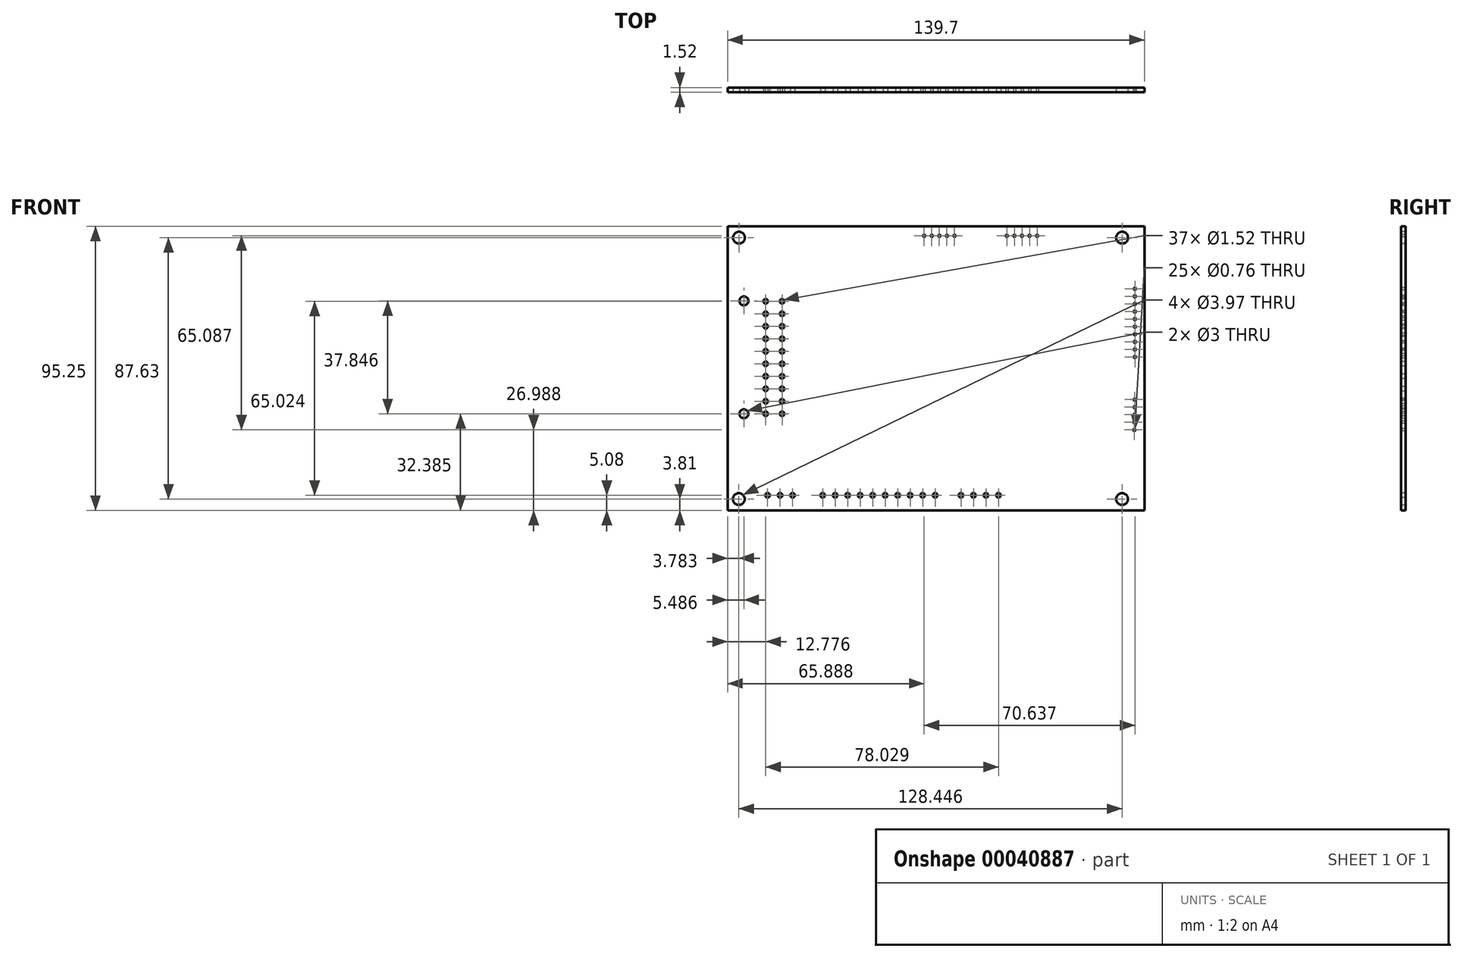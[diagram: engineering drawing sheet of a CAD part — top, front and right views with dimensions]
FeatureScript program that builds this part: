
annotation { "Feature Type Name" : "Feature", "Feature Type Description" : "" }
export const myFeature = defineFeature(function(context is Context, id is Id, definition is map)
    precondition{}
    {
        {
            var Q0;
            Q0=qCreatedBy(makeId("Front.planeOp"),FACE);
            var sketch = newSketch(context, id + "F0", { "sketchPlane" : qUnion([Q0])});
            skLineSegment(sketch, "E0.bottom", {"start": v(0, 0) * mm, "end": v(139.7, 0) * mm});
            skLineSegment(sketch, "E0.top", {"start": v(0, 95.25) * mm, "end": v(139.7, 95.25) * mm});
            skLineSegment(sketch, "E0.left", {"start": v(0, 0) * mm, "end": v(0, 95.25) * mm});
            skLineSegment(sketch, "E0.right", {"start": v(139.7, 0) * mm, "end": v(139.7, 95.25) * mm});
            skLineSegment(sketch, "E1", {"start": v(0, 47.62) * mm, "end": v(139.7, 47.62) * mm, "construction": true});
            skLineSegment(sketch, "E2", {"start": v(69.85, 95.25) * mm, "end": v(69.85, 0) * mm, "construction": true});
            skSolve(sketch);
        }
        {
            var Q0;
            Q0 = qSketchRegion(id + "F0", true);
            extrude(context, id + "F1", {"entities" : qUnion([Q0]), "depth" : 1.52 * mm});
        }
        {
            var Q0;
            Q0=makeQuery(id+"F1.opExtrude","CAP_FACE",FACE,{"disambiguationData":[OSD([sQuery(id+"F0.wireOp",EDGE,"E0.bottom"),sQuery(id+"F0.wireOp",EDGE,"E0.top"),sQuery(id+"F0.wireOp",EDGE,"E0.left"),sQuery(id+"F0.wireOp",EDGE,"E0.right")])],"isStart":false});
            var sketch = newSketch(context, id + "F2", { "sketchPlane" : qUnion([Q0])});
            skCircle(sketch, "E3", {"center": v(3.8, 91.44) * mm, "radius": 1.98 * mm});
            skCircle(sketch, "E4.1.0.0", {"center": v(132.23, 91.44) * mm, "radius": 1.98 * mm});
            skLineSegment(sketch, "E4.direction1", {"start": v(3.8, 91.44) * mm, "end": v(132.23, 91.44) * mm, "construction": true});
            skCircle(sketch, "E5.1.0.0", {"center": v(3.78, 3.81) * mm, "radius": 1.98 * mm});
            skLineSegment(sketch, "E5.direction1", {"start": v(3.8, 91.44) * mm, "end": v(3.78, 3.81) * mm, "construction": true});
            skCircle(sketch, "E6.1.0.0", {"center": v(132.21, 3.81) * mm, "radius": 1.98 * mm});
            skLineSegment(sketch, "E6.direction1", {"start": v(3.78, 3.81) * mm, "end": v(132.21, 3.81) * mm, "construction": true});
            skSolve(sketch);
        }
        {
            var Q0;
            Q0 = qSketchRegion(id + "F2", true);
            extrude(context, id + "F3", {"entities" : qUnion([Q0]), "operationType" : NewBodyOperationType.REMOVE, "oppositeDirection" : true, "depth" : 25.4 * mm});
        }
        {
            var Q0;
            Q0=makeQuery(id+"F2.imprint","IMPRINT",FACE,{"disambiguationData":[TD([[makeQuery(id+"F2.imprint","IMPRINT",EDGE,{"derivedFrom":sQuery(id+"F2.wireOp",EDGE,"E3")}),-1.0]])]});
            var sketch = newSketch(context, id + "F4", { "sketchPlane" : qUnion([Q0])});
            skCircle(sketch, "E7", {"center": v(136.53, 74.3) * mm, "radius": 0.38 * mm});
            skCircle(sketch, "E8.0.1.0", {"center": v(136.53, 71.75) * mm, "radius": 0.38 * mm});
            skCircle(sketch, "E8.0.2.0", {"center": v(136.53, 69.22) * mm, "radius": 0.38 * mm});
            skCircle(sketch, "E8.0.3.0", {"center": v(136.53, 66.67) * mm, "radius": 0.38 * mm});
            skCircle(sketch, "E8.0.4.0", {"center": v(136.53, 64.13) * mm, "radius": 0.38 * mm});
            skCircle(sketch, "E8.0.5.0", {"center": v(136.53, 61.6) * mm, "radius": 0.38 * mm});
            skCircle(sketch, "E8.0.6.0", {"center": v(136.53, 59.05) * mm, "radius": 0.38 * mm});
            skCircle(sketch, "E8.0.7.0", {"center": v(136.53, 56.51) * mm, "radius": 0.38 * mm});
            skCircle(sketch, "E8.0.8.0", {"center": v(136.53, 53.97) * mm, "radius": 0.38 * mm});
            skCircle(sketch, "E8.0.9.0", {"center": v(136.53, 51.44) * mm, "radius": 0.38 * mm});
            skLineSegment(sketch, "E8.direction1", {"start": v(136.53, 74.3) * mm, "end": v(186.53, 74.3) * mm, "construction": true});
            skLineSegment(sketch, "E8.direction2", {"start": v(136.53, 74.3) * mm, "end": v(136.53, 71.75) * mm, "construction": true});
            skCircle(sketch, "E9", {"center": v(136.48, 37.15) * mm, "radius": 0.38 * mm});
            skCircle(sketch, "E10.1.0.0", {"center": v(136.45, 34.6) * mm, "radius": 0.38 * mm});
            skCircle(sketch, "E10.2.0.0", {"center": v(136.41, 32.07) * mm, "radius": 0.38 * mm});
            skCircle(sketch, "E10.3.0.0", {"center": v(136.38, 29.53) * mm, "radius": 0.38 * mm});
            skCircle(sketch, "E10.4.0.0", {"center": v(136.35, 26.99) * mm, "radius": 0.38 * mm});
            skLineSegment(sketch, "E10.direction1", {"start": v(136.48, 37.15) * mm, "end": v(136.45, 34.6) * mm, "construction": true});
            skCircle(sketch, "E11", {"center": v(103.76, 92.08) * mm, "radius": 0.38 * mm});
            skCircle(sketch, "E12.1.0.0", {"center": v(101.22, 92.08) * mm, "radius": 0.38 * mm});
            skCircle(sketch, "E12.2.0.0", {"center": v(98.68, 92.08) * mm, "radius": 0.38 * mm});
            skLineSegment(sketch, "E12.direction1", {"start": v(103.76, 92.08) * mm, "end": v(101.22, 92.08) * mm, "construction": true});
            skCircle(sketch, "E13.0.3.0", {"center": v(96.14, 92.08) * mm, "radius": 0.38 * mm});
            skCircle(sketch, "E13.0.4.0", {"center": v(93.6, 92.08) * mm, "radius": 0.38 * mm});
            skCircle(sketch, "E14", {"center": v(76.05, 92.08) * mm, "radius": 0.38 * mm});
            skCircle(sketch, "E15.1.0.0", {"center": v(73.5, 92.08) * mm, "radius": 0.38 * mm});
            skCircle(sketch, "E15.2.0.0", {"center": v(70.97, 92.08) * mm, "radius": 0.38 * mm});
            skCircle(sketch, "E15.3.0.0", {"center": v(68.43, 92.08) * mm, "radius": 0.38 * mm});
            skCircle(sketch, "E15.4.0.0", {"center": v(65.89, 92.08) * mm, "radius": 0.38 * mm});
            skLineSegment(sketch, "E15.direction1", {"start": v(76.05, 92.08) * mm, "end": v(73.5, 92.08) * mm, "construction": true});
            skCircle(sketch, "E16", {"center": v(90.8, 5.08) * mm, "radius": 0.76 * mm});
            skCircle(sketch, "E17.1.0.0", {"center": v(86.61, 5.08) * mm, "radius": 0.76 * mm});
            skCircle(sketch, "E17.2.0.0", {"center": v(82.42, 5.08) * mm, "radius": 0.76 * mm});
            skCircle(sketch, "E17.3.0.0", {"center": v(78.23, 5.08) * mm, "radius": 0.76 * mm});
            skLineSegment(sketch, "E17.direction1", {"start": v(90.8, 5.08) * mm, "end": v(86.61, 5.08) * mm, "construction": true});
            skCircle(sketch, "E18", {"center": v(69.6, 5.08) * mm, "radius": 0.76 * mm});
            skCircle(sketch, "E19.1.0.0", {"center": v(65.4, 5.08) * mm, "radius": 0.76 * mm});
            skCircle(sketch, "E19.2.0.0", {"center": v(61.21, 5.08) * mm, "radius": 0.76 * mm});
            skCircle(sketch, "E19.3.0.0", {"center": v(57.02, 5.08) * mm, "radius": 0.76 * mm});
            skCircle(sketch, "E19.4.0.0", {"center": v(52.83, 5.08) * mm, "radius": 0.76 * mm});
            skCircle(sketch, "E19.5.0.0", {"center": v(48.64, 5.08) * mm, "radius": 0.76 * mm});
            skCircle(sketch, "E19.6.0.0", {"center": v(44.45, 5.08) * mm, "radius": 0.76 * mm});
            skCircle(sketch, "E19.7.0.0", {"center": v(40.26, 5.08) * mm, "radius": 0.76 * mm});
            skCircle(sketch, "E19.8.0.0", {"center": v(36.07, 5.08) * mm, "radius": 0.76 * mm});
            skCircle(sketch, "E19.9.0.0", {"center": v(31.88, 5.08) * mm, "radius": 0.76 * mm});
            skLineSegment(sketch, "E19.direction1", {"start": v(69.6, 5.08) * mm, "end": v(65.4, 5.08) * mm, "construction": true});
            skCircle(sketch, "E20", {"center": v(21.8, 5.08) * mm, "radius": 0.76 * mm});
            skCircle(sketch, "E21.1.0.0", {"center": v(17.6, 5.08) * mm, "radius": 0.76 * mm});
            skCircle(sketch, "E21.2.0.0", {"center": v(13.42, 5.08) * mm, "radius": 0.76 * mm});
            skLineSegment(sketch, "E21.direction1", {"start": v(21.8, 5.08) * mm, "end": v(17.6, 5.08) * mm, "construction": true});
            skCircle(sketch, "E22", {"center": v(18.29, 32.39) * mm, "radius": 0.76 * mm});
            skCircle(sketch, "E23.0.1.0", {"center": v(18.29, 36.58) * mm, "radius": 0.76 * mm});
            skCircle(sketch, "E23.0.2.0", {"center": v(18.29, 40.77) * mm, "radius": 0.76 * mm});
            skCircle(sketch, "E23.0.3.0", {"center": v(18.29, 44.96) * mm, "radius": 0.76 * mm});
            skCircle(sketch, "E23.0.4.0", {"center": v(18.29, 49.15) * mm, "radius": 0.76 * mm});
            skCircle(sketch, "E23.0.5.0", {"center": v(18.29, 53.34) * mm, "radius": 0.76 * mm});
            skCircle(sketch, "E23.0.6.0", {"center": v(18.29, 57.53) * mm, "radius": 0.76 * mm});
            skCircle(sketch, "E23.0.7.0", {"center": v(18.29, 61.72) * mm, "radius": 0.76 * mm});
            skCircle(sketch, "E23.0.8.0", {"center": v(18.29, 65.91) * mm, "radius": 0.76 * mm});
            skCircle(sketch, "E23.0.9.0", {"center": v(18.29, 70.1) * mm, "radius": 0.76 * mm});
            skCircle(sketch, "E23.1.0.0", {"center": v(12.78, 32.39) * mm, "radius": 0.76 * mm});
            skCircle(sketch, "E23.1.1.0", {"center": v(12.78, 36.58) * mm, "radius": 0.76 * mm});
            skCircle(sketch, "E23.1.2.0", {"center": v(12.78, 40.77) * mm, "radius": 0.76 * mm});
            skCircle(sketch, "E23.1.3.0", {"center": v(12.78, 44.96) * mm, "radius": 0.76 * mm});
            skCircle(sketch, "E23.1.4.0", {"center": v(12.78, 49.15) * mm, "radius": 0.76 * mm});
            skCircle(sketch, "E23.1.5.0", {"center": v(12.78, 53.34) * mm, "radius": 0.76 * mm});
            skCircle(sketch, "E23.1.6.0", {"center": v(12.78, 57.53) * mm, "radius": 0.76 * mm});
            skCircle(sketch, "E23.1.7.0", {"center": v(12.78, 61.72) * mm, "radius": 0.76 * mm});
            skCircle(sketch, "E23.1.8.0", {"center": v(12.78, 65.91) * mm, "radius": 0.76 * mm});
            skCircle(sketch, "E23.1.9.0", {"center": v(12.78, 70.1) * mm, "radius": 0.76 * mm});
            skLineSegment(sketch, "E23.direction1", {"start": v(18.29, 32.39) * mm, "end": v(12.78, 32.39) * mm, "construction": true});
            skLineSegment(sketch, "E23.direction2", {"start": v(18.29, 32.39) * mm, "end": v(18.29, 36.58) * mm, "construction": true});
            skCircle(sketch, "E24", {"center": v(5.49, 32.39) * mm, "radius": 1.5 * mm});
            skCircle(sketch, "E25", {"center": v(5.49, 70.23) * mm, "radius": 1.5 * mm});
            skSolve(sketch);
        }
        {
            var Q0;
            Q0 = qSketchRegion(id + "F4", true);
            extrude(context, id + "F5", {"entities" : qUnion([Q0]), "operationType" : NewBodyOperationType.REMOVE, "endBound" : BoundingType.THROUGH_ALL, "oppositeDirection" : true, "depth" : 25.4 * mm});
        }
    });
